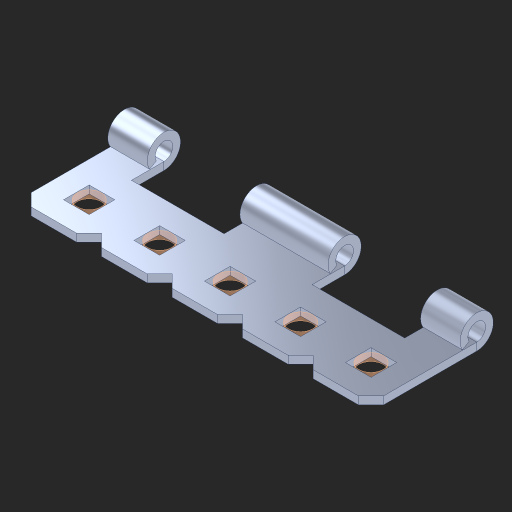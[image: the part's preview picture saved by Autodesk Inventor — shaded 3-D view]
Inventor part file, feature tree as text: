
AUTODESK INVENTOR PART (.ipt)
format: ipt  version: 2023 (Build 270158000, 158)  size: 211,456 bytes
history: native  units: in
note: dims shown in document units (in); Inventor stores cm internally (conversion verified against a paired STEP export)
features: other x7, extrude x5, pattern_linear x1, imported_body x1, sketch x1
ambient origin geometry x8: Origin, YZ Plane, XZ Plane, XY Plane, X Axis, Y Axis, Z Axis, Center Point
bodies: Body1 (feature_tree), Body2 (feature_tree), Body3 (feature_tree), Body4 (feature_tree), Body5 (feature_tree), Body6 (feature_tree)
feature tree (15):
  other  "Cut-Extrude3"
  other  "Top"
  pattern_linear  "Rectangular Pattern1"  Count1=5 Spacing1=0.5in
  imported_body  "Base1"
  sketch  "Sketch1"  dims[d15=0.046in d16=0.0in d17=1.9685in d19=0.5in d30=0.172in]
  other  "Srf1"
  other  "Srf2"
  other  "Srf3"
  other  "Srf4"
  other  "Srf5"
  extrude  "ExtrusionSrf1"  Depth=0.5in
  extrude  "ExtrusionSrf2"  [1 undecoded]
  extrude  "ExtrusionSrf3"  [1 undecoded]
  extrude  "ExtrusionSrf4"  [1 undecoded]
  extrude  "ExtrusionSrf5"  [1 undecoded]
note: 4 required parameter values undecoded (feature->parameter linkage not recoverable at this tier; creation-order binding heuristic only, values carry confidence <= 0.55)
